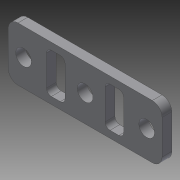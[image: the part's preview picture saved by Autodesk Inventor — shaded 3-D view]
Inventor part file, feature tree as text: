
AUTODESK INVENTOR PART (.ipt)
format: ipt  version: 2015 (Build 190159000, 159)  size: 125,440 bytes
history: native  units: in
note: dims shown in document units (in); Inventor stores cm internally (conversion verified against a paired STEP export)
features: extrude x1, sketch x1
ambient origin geometry x8: Origin, YZ Plane, XZ Plane, XY Plane, X Axis, Y Axis, Z Axis, Center Point
bodies: Solid1 (feature_tree)
feature tree (2):
  extrude  "Extrusion1"  Depth=1.378in
  sketch  "Sketch1"  dims[d0=3.937in d1=1.378in d2=3.1496in d3=0.4016in d4=0.25in d5=0.0in d6=0.4016in d7=0.25in d8=1.0236in d9=0.4764in d10=0.125in d11=1.5in]
